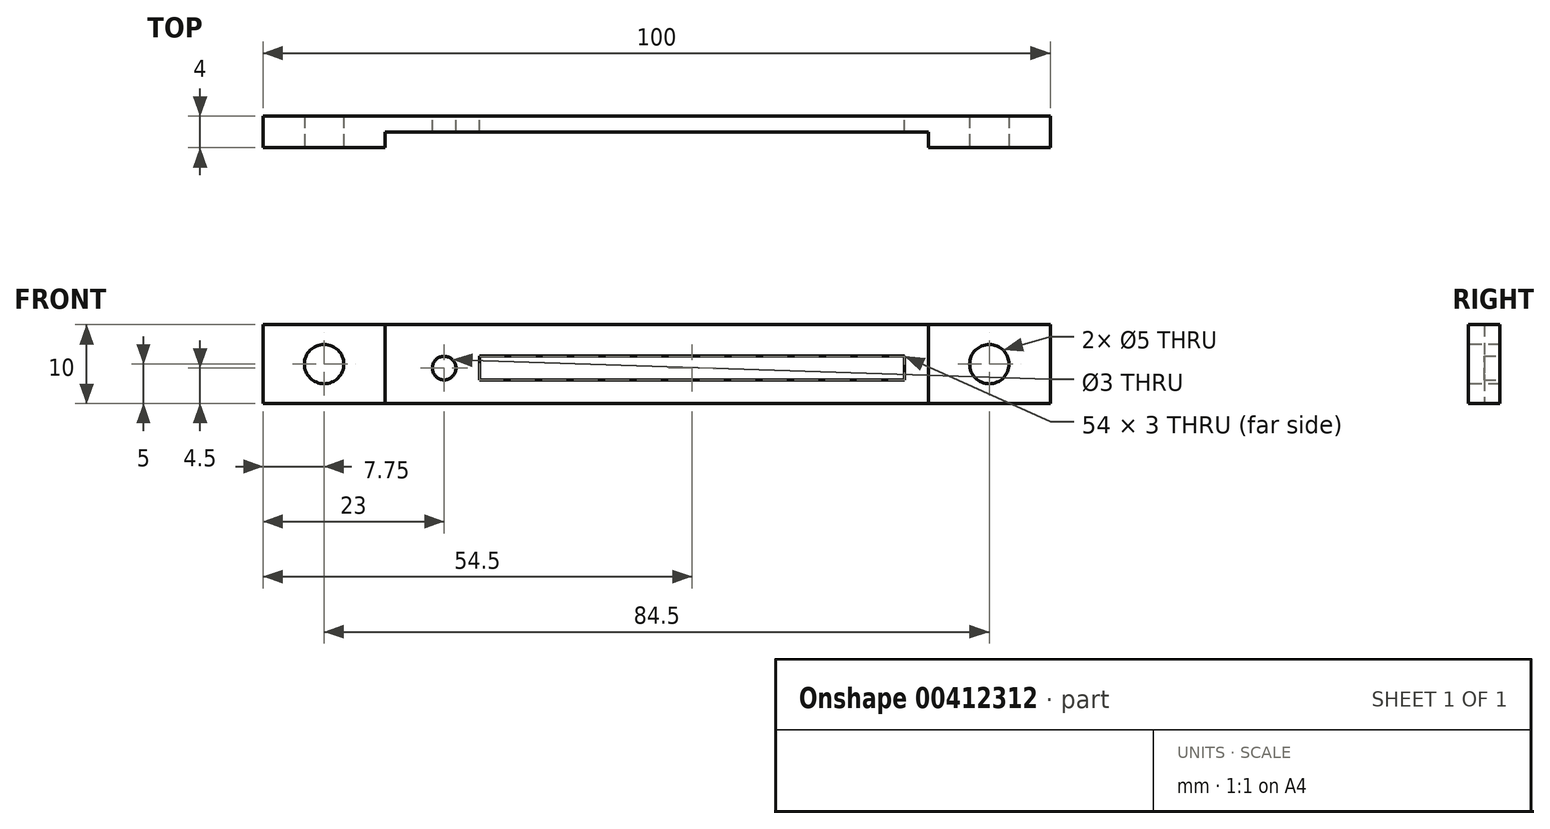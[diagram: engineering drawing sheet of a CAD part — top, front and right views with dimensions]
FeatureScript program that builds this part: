
annotation { "Feature Type Name" : "Feature", "Feature Type Description" : "" }
export const myFeature = defineFeature(function(context is Context, id is Id, definition is map)
    precondition{}
    {
        {
            var Q0;
            Q0=qCreatedBy(makeId("Front.planeOp"),FACE);
            var sketch = newSketch(context, id + "F0", { "sketchPlane" : qUnion([Q0])});
            skLineSegment(sketch, "E0.bottom", {"start": v(50, 5) * mm, "end": v(-50, 5) * mm});
            skLineSegment(sketch, "E0.top", {"start": v(50, -5) * mm, "end": v(-50, -5) * mm});
            skLineSegment(sketch, "E0.left", {"start": v(50, 5) * mm, "end": v(50, -5) * mm});
            skLineSegment(sketch, "E0.right", {"start": v(-50, 5) * mm, "end": v(-50, -5) * mm});
            skPoint(sketch, "E0.middle", {"position": v(0, 0) * mm});
            skLineSegment(sketch, "E1.bottom", {"start": v(31.5, 1) * mm, "end": v(-31.5, 1) * mm});
            skLineSegment(sketch, "E1.top", {"start": v(31.5, -2) * mm, "end": v(-31.5, -2) * mm});
            skLineSegment(sketch, "E1.left", {"start": v(31.5, 1) * mm, "end": v(31.5, -2) * mm});
            skLineSegment(sketch, "E1.right", {"start": v(-31.5, 1) * mm, "end": v(-31.5, -2) * mm});
            skPoint(sketch, "E1.middle", {"position": v(0, -0.5) * mm});
            skSolve(sketch);
        }
        {
            var Q0;
            Q0 = qSketchRegion(id + "F0", true);
            extrude(context, id + "F1", {"entities" : qUnion([Q0]), "depth" : 4 * mm});
        }
        {
            var Q0;
            Q0=makeQuery(id+"F1.opExtrude","CAP_FACE",FACE,{"disambiguationData":[OSD([sQuery(id+"F0.wireOp",EDGE,"E0.bottom"),sQuery(id+"F0.wireOp",EDGE,"E0.top"),sQuery(id+"F0.wireOp",EDGE,"E0.left"),sQuery(id+"F0.wireOp",EDGE,"E0.right"),sQuery(id+"F0.wireOp",EDGE,"E1.bottom"),sQuery(id+"F0.wireOp",EDGE,"E1.top"),sQuery(id+"F0.wireOp",EDGE,"E1.left"),sQuery(id+"F0.wireOp",EDGE,"E1.right")])],"isStart":false});
            var sketch = newSketch(context, id + "F2", { "sketchPlane" : qUnion([Q0])});
            skLineSegment(sketch, "E2.bottom", {"start": v(34.5, 5) * mm, "end": v(-34.5, 5) * mm});
            skLineSegment(sketch, "E2.top", {"start": v(34.5, -5) * mm, "end": v(-34.5, -5) * mm});
            skLineSegment(sketch, "E2.left", {"start": v(34.5, 5) * mm, "end": v(34.5, -5) * mm});
            skLineSegment(sketch, "E2.right", {"start": v(-34.5, 5) * mm, "end": v(-34.5, -5) * mm});
            skPoint(sketch, "E2.middle", {"position": v(0, 0) * mm});
            skSolve(sketch);
        }
        {
            var Q0;
            Q0 = qSketchRegion(id + "F2", true);
            extrude(context, id + "F3", {"entities" : qUnion([Q0]), "operationType" : NewBodyOperationType.REMOVE, "oppositeDirection" : true, "depth" : 2 * mm});
        }
        {
            var Q0;
            {var subQ0=sQuery(id+"F0.wireOp",EDGE,"E0.bottom");var subQ1=sQuery(id+"F0.wireOp",EDGE,"E0.right");var subQ2=sQuery(id+"F0.wireOp",EDGE,"E0.top");Q0=makeQuery(id+"F3.boolean.opBoolean","SPLIT",FACE,{"disambiguationData":[TD([makeQuery(id+"F1.opExtrude","SWEPT_FACE",FACE,{"disambiguationData":[OSD([subQ1])]})])],"derivedFrom":makeQuery(id+"F1.opExtrude","CAP_FACE",FACE,{"disambiguationData":[OSD([subQ0,subQ2,sQuery(id+"F0.wireOp",EDGE,"E0.left"),subQ1,sQuery(id+"F0.wireOp",EDGE,"E1.bottom"),sQuery(id+"F0.wireOp",EDGE,"E1.top"),sQuery(id+"F0.wireOp",EDGE,"E1.left"),sQuery(id+"F0.wireOp",EDGE,"E1.right")])],"isStart":false})});}
            var sketch = newSketch(context, id + "F4", { "sketchPlane" : qUnion([Q0])});
            skLineSegment(sketch, "E3", {"start": v(-50, 5) * mm, "end": v(-34.5, -5) * mm, "construction": true});
            skCircle(sketch, "E4", {"center": v(-42.25, 0) * mm, "radius": 2.5 * mm});
            skSolve(sketch);
        }
        {
            var Q0;
            Q0 = qSketchRegion(id + "F4", true);
            extrude(context, id + "F5", {"entities" : qUnion([Q0]), "operationType" : NewBodyOperationType.REMOVE, "oppositeDirection" : true, "depth" : 25 * mm});
        }
        {
            var Q0;
            {var subQ0=sQuery(id+"F0.wireOp",EDGE,"E0.bottom");var subQ1=sQuery(id+"F0.wireOp",EDGE,"E0.top");var subQ2=sQuery(id+"F0.wireOp",EDGE,"E0.left");Q0=makeQuery(id+"F3.boolean.opBoolean","SPLIT",FACE,{"disambiguationData":[TD([makeQuery(id+"F1.opExtrude","SWEPT_FACE",FACE,{"disambiguationData":[OSD([subQ2])]})])],"derivedFrom":makeQuery(id+"F1.opExtrude","CAP_FACE",FACE,{"disambiguationData":[OSD([subQ0,subQ1,subQ2,sQuery(id+"F0.wireOp",EDGE,"E0.right"),sQuery(id+"F0.wireOp",EDGE,"E1.bottom"),sQuery(id+"F0.wireOp",EDGE,"E1.top"),sQuery(id+"F0.wireOp",EDGE,"E1.left"),sQuery(id+"F0.wireOp",EDGE,"E1.right")])],"isStart":false})});}
            var sketch = newSketch(context, id + "F6", { "sketchPlane" : qUnion([Q0])});
            skLineSegment(sketch, "E5", {"start": v(34.5, 5) * mm, "end": v(50, -5) * mm, "construction": true});
            skCircle(sketch, "E6", {"center": v(42.25, 0) * mm, "radius": 2.5 * mm});
            skSolve(sketch);
        }
        {
            var Q0;
            Q0 = qSketchRegion(id + "F6", true);
            extrude(context, id + "F7", {"entities" : qUnion([Q0]), "operationType" : NewBodyOperationType.REMOVE, "oppositeDirection" : true, "depth" : 25 * mm});
        }
        {
            var Q0;
            Q0=makeQuery(id+"F1.opExtrude","CAP_FACE",FACE,{"disambiguationData":[OSD([sQuery(id+"F0.wireOp",EDGE,"E0.bottom"),sQuery(id+"F0.wireOp",EDGE,"E0.top"),sQuery(id+"F0.wireOp",EDGE,"E0.left"),sQuery(id+"F0.wireOp",EDGE,"E0.right"),sQuery(id+"F0.wireOp",EDGE,"E1.bottom"),sQuery(id+"F0.wireOp",EDGE,"E1.top"),sQuery(id+"F0.wireOp",EDGE,"E1.left"),sQuery(id+"F0.wireOp",EDGE,"E1.right")])],"isStart":true});
            var sketch = newSketch(context, id + "F8", { "sketchPlane" : qUnion([Q0])});
            skLineSegment(sketch, "E7.bottom", {"start": v(31.5, 1) * mm, "end": v(22.5, 1) * mm});
            skLineSegment(sketch, "E7.top", {"start": v(31.5, -2) * mm, "end": v(22.5, -2) * mm});
            skLineSegment(sketch, "E7.left", {"start": v(31.5, 1) * mm, "end": v(31.5, -2) * mm});
            skLineSegment(sketch, "E7.right", {"start": v(22.5, 1) * mm, "end": v(22.5, -2) * mm});
            skSolve(sketch);
        }
        {
            var Q0;
            Q0 = qSketchRegion(id + "F8", true);
            extrude(context, id + "F9", {"entities" : qUnion([Q0]), "operationType" : NewBodyOperationType.ADD, "oppositeDirection" : true, "depth" : 2 * mm});
        }
        {
            var Q0;
            Q0=makeQuery(id+"F9.boolean.opBoolean","MERGE",FACE,{"derivedFrom":[makeQuery(id+"F1.opExtrude","CAP_FACE",FACE,{"disambiguationData":[OSD([sQuery(id+"F0.wireOp",EDGE,"E0.bottom"),sQuery(id+"F0.wireOp",EDGE,"E0.top"),sQuery(id+"F0.wireOp",EDGE,"E0.left"),sQuery(id+"F0.wireOp",EDGE,"E0.right"),sQuery(id+"F0.wireOp",EDGE,"E1.bottom"),sQuery(id+"F0.wireOp",EDGE,"E1.top"),sQuery(id+"F0.wireOp",EDGE,"E1.left"),sQuery(id+"F0.wireOp",EDGE,"E1.right")])],"isStart":true}),makeQuery(id+"F9.opExtrude","CAP_FACE",FACE,{"disambiguationData":[OSD([sQuery(id+"F8.wireOp",EDGE,"E7.bottom"),sQuery(id+"F8.wireOp",EDGE,"E7.top"),sQuery(id+"F8.wireOp",EDGE,"E7.left"),sQuery(id+"F8.wireOp",EDGE,"E7.right")])],"isStart":true})]});
            var sketch = newSketch(context, id + "F10", { "sketchPlane" : qUnion([Q0])});
            skCircle(sketch, "E8", {"center": v(27, -0.5) * mm, "radius": 1.5 * mm});
            skSolve(sketch);
        }
        {
            var Q0;
            Q0 = qSketchRegion(id + "F10", true);
            extrude(context, id + "F11", {"entities" : qUnion([Q0]), "operationType" : NewBodyOperationType.REMOVE, "oppositeDirection" : true, "depth" : 25 * mm});
        }
    });
